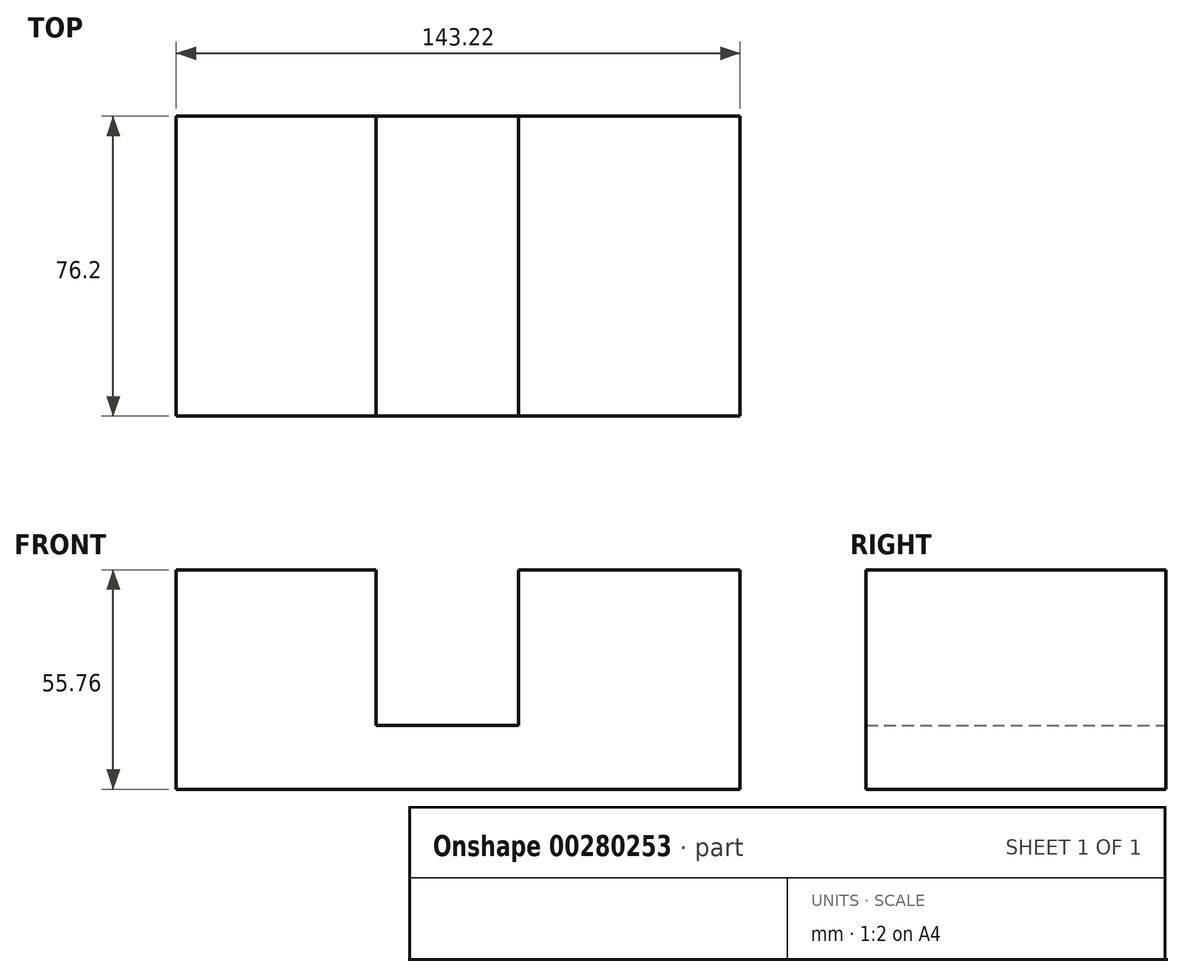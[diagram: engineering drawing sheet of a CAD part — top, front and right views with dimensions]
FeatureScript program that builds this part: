
annotation { "Feature Type Name" : "Feature", "Feature Type Description" : "" }
export const myFeature = defineFeature(function(context is Context, id is Id, definition is map)
    precondition{}
    {
        {
            var Q0;
            Q0=qCreatedBy(makeId("Front.planeOp"),FACE);
            var sketch = newSketch(context, id + "F0", { "sketchPlane" : qUnion([Q0])});
            skLineSegment(sketch, "E0", {"start": v(-67.03, 55.76) * mm, "end": v(-16.23, 55.76) * mm});
            skLineSegment(sketch, "E1", {"start": v(-16.23, 55.76) * mm, "end": v(-16.23, 16.23) * mm});
            skLineSegment(sketch, "E2", {"start": v(-16.23, 16.23) * mm, "end": v(19.86, 16.23) * mm});
            skLineSegment(sketch, "E3", {"start": v(19.86, 16.23) * mm, "end": v(19.86, 55.76) * mm});
            skLineSegment(sketch, "E4", {"start": v(19.86, 55.76) * mm, "end": v(70.66, 55.76) * mm});
            skLineSegment(sketch, "E5", {"start": v(-67.03, 55.76) * mm, "end": v(-67.03, 0) * mm});
            skLineSegment(sketch, "E6", {"start": v(-67.03, 0) * mm, "end": v(76.2, 0) * mm});
            skLineSegment(sketch, "E7", {"start": v(76.2, 0) * mm, "end": v(76.2, 55.76) * mm});
            skLineSegment(sketch, "E8", {"start": v(76.2, 55.76) * mm, "end": v(70.66, 55.76) * mm});
            skSolve(sketch);
        }
        {
            var Q0;
            Q0 = qSketchRegion(id + "F0", true);
            extrude(context, id + "F1", {"entities" : qUnion([Q0]), "depth" : 76.2 * mm});
        }
    });
